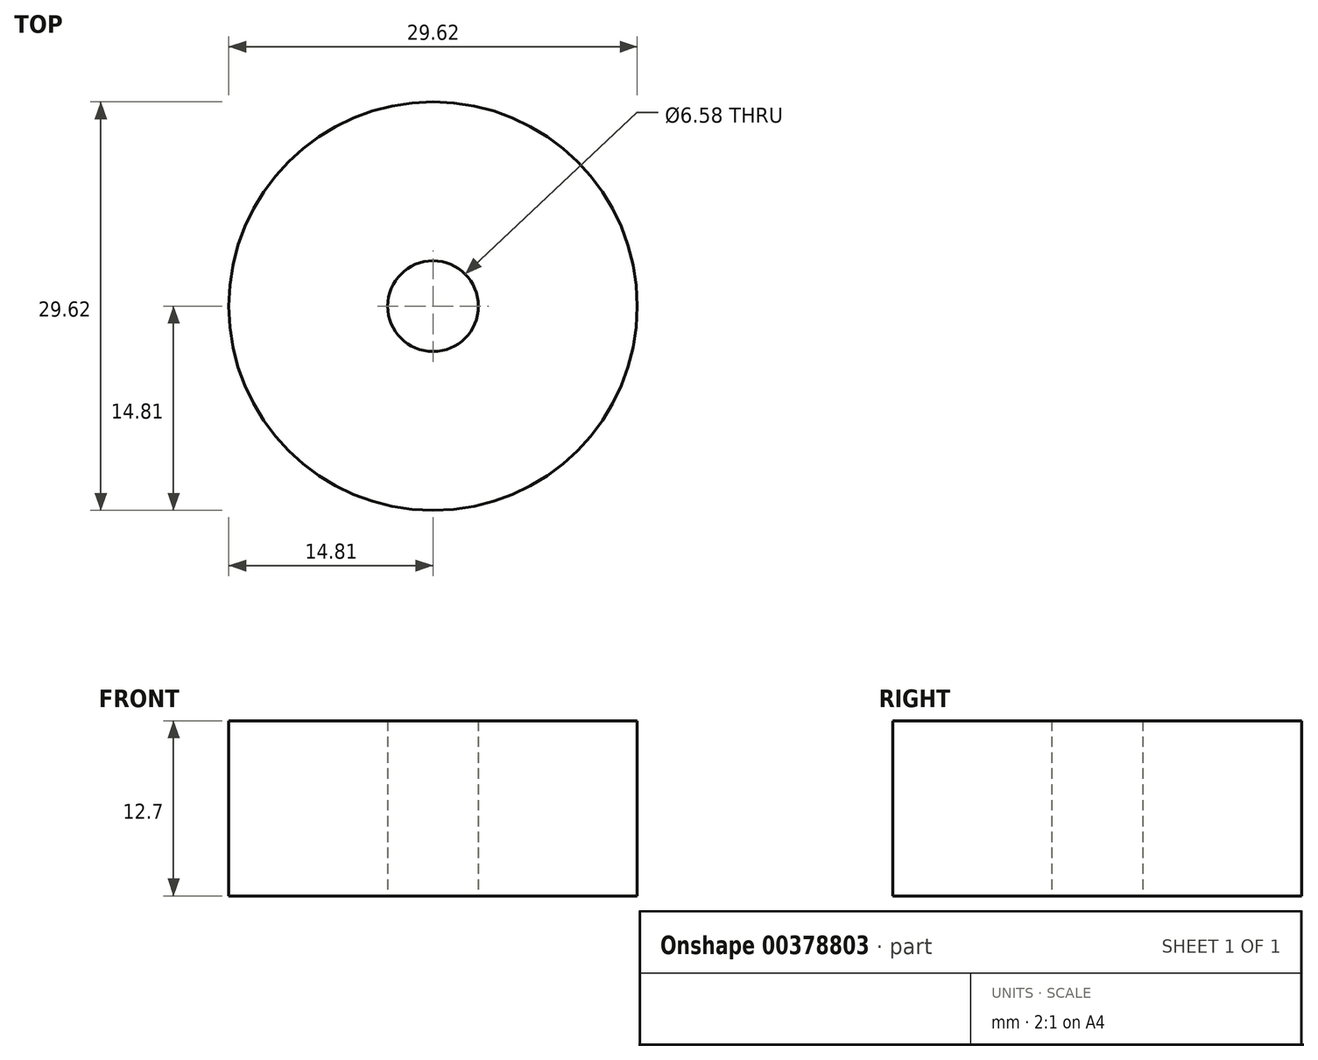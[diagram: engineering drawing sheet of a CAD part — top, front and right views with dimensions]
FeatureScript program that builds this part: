
annotation { "Feature Type Name" : "Feature", "Feature Type Description" : "" }
export const myFeature = defineFeature(function(context is Context, id is Id, definition is map)
    precondition{}
    {
        {
            var Q0;
            Q0=qCreatedBy(makeId("Top.planeOp"),FACE);
            var sketch = newSketch(context, id + "F0", { "sketchPlane" : qUnion([Q0])});
            skCircle(sketch, "E0", {"center": v(0, 0) * mm, "radius": 14.81 * mm});
            skCircle(sketch, "E1", {"center": v(0, 0) * mm, "radius": 3.29 * mm});
            skSolve(sketch);
        }
        {
            var Q0;
            Q0=makeQuery(id+"F0.imprint","IMPRINT",FACE,{"disambiguationData":[TD([[makeQuery(id+"F0.imprint","IMPRINT",EDGE,{"derivedFrom":sQuery(id+"F0.wireOp",EDGE,"E0")}),1.0]])]});
            extrude(context, id + "F1", {"entities" : qUnion([Q0]), "depth" : 12.7 * mm});
        }
    });
